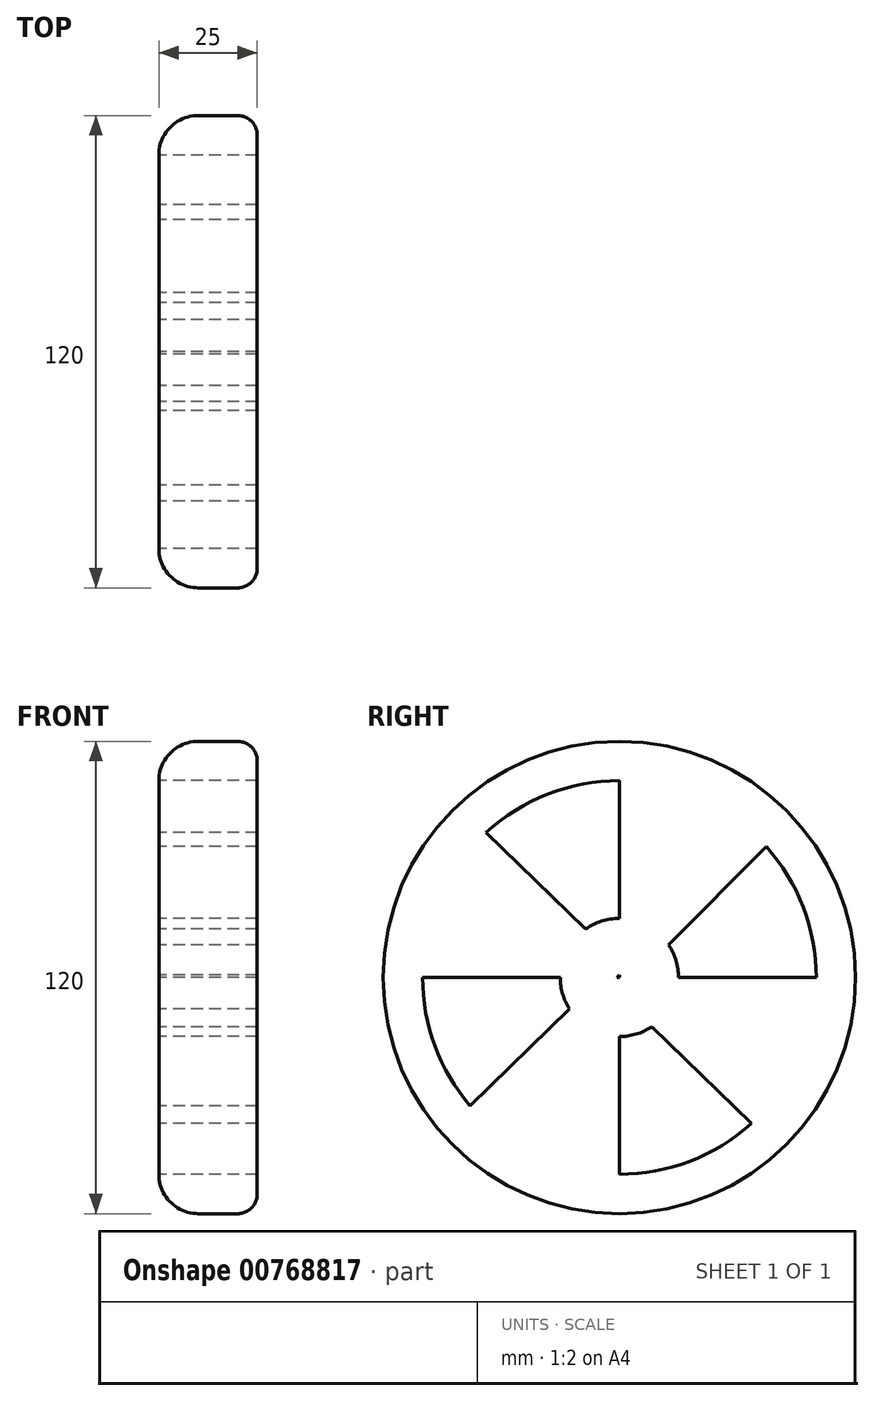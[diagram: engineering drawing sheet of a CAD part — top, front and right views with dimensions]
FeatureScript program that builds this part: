
annotation { "Feature Type Name" : "Feature", "Feature Type Description" : "" }
export const myFeature = defineFeature(function(context is Context, id is Id, definition is map)
    precondition{}
    {
        {
            var Q0;
            Q0=qCreatedBy(makeId("Right.planeOp"),FACE);
            var sketch = newSketch(context, id + "F0", { "sketchPlane" : qUnion([Q0])});
            skCircle(sketch, "E0", {"center": v(0, 0) * mm, "radius": 60 * mm});
            skCircle(sketch, "E1", {"center": v(0, 0) * mm, "radius": 55 * mm});
            skCircle(sketch, "E2", {"center": v(0, 0) * mm, "radius": 50 * mm});
            skLineSegment(sketch, "E3", {"start": v(0, 50) * mm, "end": v(0, 15) * mm});
            skLineSegment(sketch, "E4", {"start": v(-50, 0) * mm, "end": v(-15, 0) * mm});
            skLineSegment(sketch, "E5", {"start": v(34.92, 35.78) * mm, "end": v(10.27, 10.94) * mm});
            skLineSegment(sketch, "E6", {"start": v(-35.91, 34.79) * mm, "end": v(-10.76, 10.45) * mm});
            skCircle(sketch, "E7", {"center": v(0, 0) * mm, "radius": 15 * mm});
            skLineSegment(sketch, "E8.trimOffspring", {"start": v(0, 0.6) * mm, "end": v(-0.6, 0) * mm});
            skLineSegment(sketch, "E9.trimOffspring", {"start": v(-0.28, 0.31) * mm, "end": v(0.04, 0) * mm});
            skLineSegment(sketch, "E10.trimOffspring", {"start": v(-10.86, -10.35) * mm, "end": v(-35.52, -35.2) * mm});
            skLineSegment(sketch, "E11.trimOffspring", {"start": v(10.8, -10.41) * mm, "end": v(35.95, -34.75) * mm});
            skLineSegment(sketch, "E12", {"start": v(-33.86, 36.8) * mm, "end": v(-8.56, 12.32) * mm});
            skLineSegment(sketch, "E13", {"start": v(3.05, 49.9) * mm, "end": v(3.05, 14.69) * mm});
            skLineSegment(sketch, "E14", {"start": v(37.33, 33.26) * mm, "end": v(12.52, 8.26) * mm});
            skLineSegment(sketch, "E15", {"start": v(33.55, -37.07) * mm, "end": v(8.22, -12.55) * mm});
            skLineSegment(sketch, "E16", {"start": v(-37.9, -32.62) * mm, "end": v(-12.69, -8) * mm});
            skLineSegment(sketch, "E17.trimOffspring", {"start": v(0, 0.6) * mm, "end": v(0, 0) * mm});
            skLineSegment(sketch, "E18.trimOffspring", {"start": v(0, -15) * mm, "end": v(0, -50) * mm});
            skLineSegment(sketch, "E19.trimOffspring", {"start": v(15, 0) * mm, "end": v(50, 0) * mm});
            skLineSegment(sketch, "E20.trimOffspring", {"start": v(-0.6, 0) * mm, "end": v(0.04, 0) * mm});
            skSolve(sketch);
        }
        {
            var Q0;
            Q0=makeQuery(id+"F0.imprint","IMPRINT",FACE,{"disambiguationData":[TD([[makeQuery(id+"F0.imprint","IMPRINT",EDGE,{"derivedFrom":sQuery(id+"F0.wireOp",EDGE,"E2")}),1.0]])]});
            var Q1;
            Q1=makeQuery(id+"F0.imprint","IMPRINT",FACE,{"disambiguationData":[TD([[makeQuery(id+"F0.imprint","IMPRINT",EDGE,{"derivedFrom":sQuery(id+"F0.wireOp",EDGE,"E1")}),1.0]])]});
            var Q2;
            Q2=makeQuery(id+"F0.imprint","IMPRINT",FACE,{"disambiguationData":[TD([[makeQuery(id+"F0.imprint","IMPRINT",EDGE,{"derivedFrom":sQuery(id+"F0.wireOp",EDGE,"E0")}),1.0]])]});
            extrude(context, id + "F1", {"entities" : qUnion([Q0, Q1, Q2]), "depth" : 25 * mm, "offsetDistance" : 25 * mm});
        }
        {
            var Q0;
            Q0=makeQuery(id+"F1.opExtrude","CAP_EDGE",EDGE,{"disambiguationData":[OSD([sQuery(id+"F0.wireOp",EDGE,"E0")])],"isStart":false});
            fillet(context, id + "F2", {"entities" : qUnion([Q0]), "radius" : 5 * mm, "tangentPropagation" : true, "allowEdgeOverflow" : false});
        }
        {
            var Q0;
            Q0=makeQuery(id+"F1.opExtrude","CAP_EDGE",EDGE,{"disambiguationData":[OSD([sQuery(id+"F0.wireOp",EDGE,"E0")])],"isStart":true});
            fillet(context, id + "F3", {"entities" : qUnion([Q0]), "radius" : 10 * mm, "tangentPropagation" : true, "allowEdgeOverflow" : false});
        }
        {
            var Q0;
            {var subQ0=sQuery(id+"F0.wireOp",EDGE,"E3");Q0=makeQuery(id+"F0.imprint","IMPRINT",FACE,{"disambiguationData":[TD([[makeQuery(id+"F0.imprint","IMPRINT",EDGE,{"derivedFrom":subQ0}),-1.0]])]});}
            var Q1;
            {var subQ0=sQuery(id+"F0.wireOp",EDGE,"E4");Q1=makeQuery(id+"F0.imprint","IMPRINT",FACE,{"disambiguationData":[TD([[makeQuery(id+"F0.imprint","IMPRINT",EDGE,{"derivedFrom":subQ0}),-1.0]])]});}
            var Q2;
            {var subQ0=sQuery(id+"F0.wireOp",EDGE,"E15");Q2=makeQuery(id+"F0.imprint","IMPRINT",FACE,{"disambiguationData":[TD([[makeQuery(id+"F0.imprint","IMPRINT",EDGE,{"derivedFrom":subQ0}),1.0]])]});}
            var Q3;
            {var subQ0=sQuery(id+"F0.wireOp",EDGE,"E14");Q3=makeQuery(id+"F0.imprint","IMPRINT",FACE,{"disambiguationData":[TD([[makeQuery(id+"F0.imprint","IMPRINT",EDGE,{"derivedFrom":subQ0}),1.0]])]});}
            extrude(context, id + "F4", {"entities" : qUnion([Q0, Q1, Q2, Q3]), "operationType" : NewBodyOperationType.REMOVE, "endBound" : BoundingType.UP_TO_NEXT, "depth" : 25 * mm, "offsetDistance" : 25 * mm});
        }
        {
            var Q0;
            {var subQ0=sQuery(id+"F0.wireOp",EDGE,"E7");var subQ15=makeQuery(id+"F0.imprint","INTERSECT",VERTEX,{"derivedFrom":[subQ0,sQuery(id+"F0.wireOp",EDGE,"E14")]});Q0=makeQuery(id+"F0.imprint","IMPRINT",FACE,{"disambiguationData":[TD([[makeQuery(id+"F0.imprint","IMPRINT",EDGE,{"disambiguationData":[TD([[subQ15,1.0]])],"derivedFrom":subQ0}),1.0]])]});}
            extrude(context, id + "F5", {"entities" : qUnion([Q0]), "operationType" : NewBodyOperationType.ADD, "depth" : 25 * mm, "offsetDistance" : 25 * mm});
        }
    });
